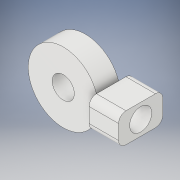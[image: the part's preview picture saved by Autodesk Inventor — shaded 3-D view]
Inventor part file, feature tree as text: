
AUTODESK INVENTOR PART (.ipt)
format: ipt  version: 2017 SP1 (Build 210196100, 196)  size: 141,824 bytes
history: native  units: in
note: dims shown in document units (in); Inventor stores cm internally (conversion verified against a paired STEP export)
features: extrude x4, sketch x4, fillet x1
ambient origin geometry x8: Origin, YZ Plane, XZ Plane, XY Plane, X Axis, Y Axis, Z Axis, Center Point
bodies: Solid1 (feature_tree)
feature tree (9):
  extrude  "Extrusion1"  Depth=0.1181in
  extrude  "Extrusion2"  Depth=0.1181in
  extrude  "Extrusion3"  Depth=0.1181in TaperAngle=0.0deg
  fillet  "Fillet1"  Radius=0.2362in
  extrude  "Extrusion4"  Depth=0.1575in TaperAngle=0.0deg
  sketch  "Sketch1"  dims[d0=0.1181in d1=0.374in]
  sketch  "Sketch2"  dims[d2=0.1181in d3=0.0in d4=0.1181in]
  sketch  "Sketch4"  dims[d5=0.0197in d6=0.1181in d7=0.0in d9=0.2362in]
  sketch  "Sketch6"  dims[d10=0.1575in d11=0.1575in d12=0.0in d13=0.0394in d14=0.1181in d15=0.1181in d16=0.0in]
